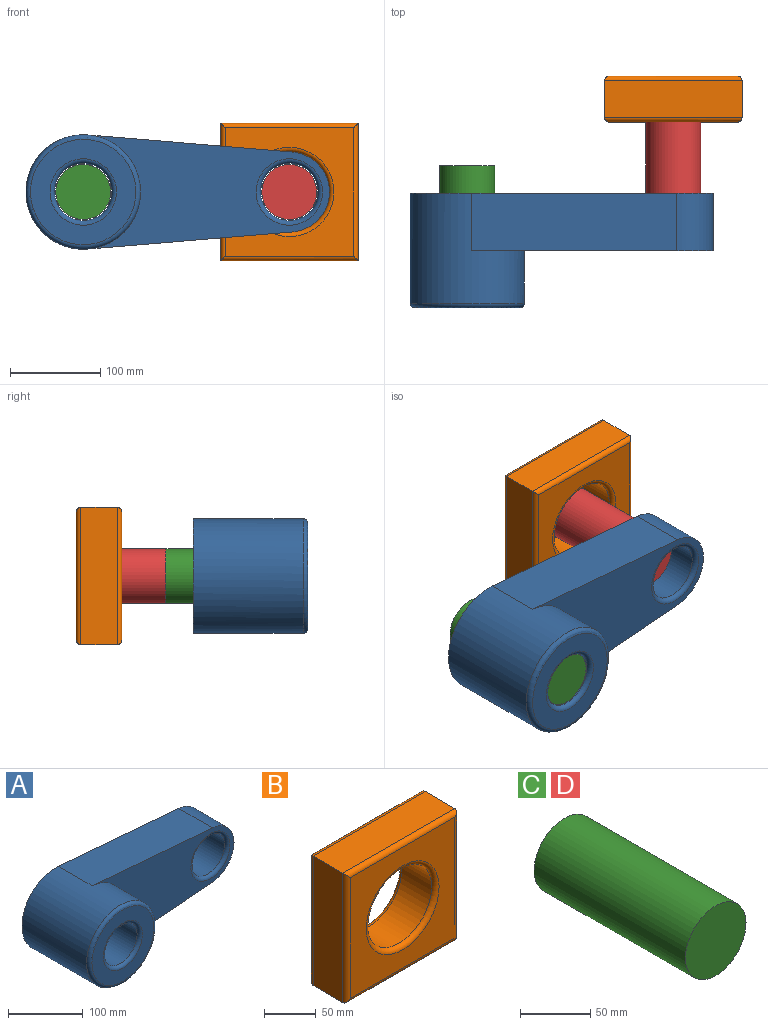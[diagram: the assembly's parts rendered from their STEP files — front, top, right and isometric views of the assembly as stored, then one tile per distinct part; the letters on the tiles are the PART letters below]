
ASSEMBLY  parts=4 mates=4
PART A: 12 faces, bbox 341.8x127x137.5 mm
  f0: plane 267.76x126.56mm, normal (0,-1,0), area 17271.4mm2, adj f1,f2,f3,f4,f11
  f1: cylinder r=63.5mm len=127mm, axis (0,1,0), area 36649.1mm2, adj f0,f2,f4,f7,f10
  f2: plane 227.01x63.5mm, normal (0.08,0,-1), area 14465.6mm2, adj f0,f1,f3,f7
  f3: cylinder r=44.45mm len=88.59mm, axis (0,1,0), area 8396.4mm2, adj f0,f2,f4,f7
  f4: plane 227.01x63.5mm, normal (0.08,0,1), area 14465.6mm2, adj f0,f1,f3,f7
  f5: cylinder r=31.75mm len=121.92mm, axis (0,1,0), area 24322mm2, adj f7,f9
  f6: cylinder r=31.75mm len=63.5mm, axis (0,1,0), area 11654.3mm2, adj f7,f11
  f7: plane 336.55x127mm, normal (0,1,0), area 27866.7mm2, adj f1,f2,f3,f4,f5,f6
  f8: plane 116.84x116.84mm, normal (0,-1,0), area 6460.5mm2, adj f9,f10
  f9: torus R=36.83mm, axis (0,-1,0), area 1684.4mm2, adj f5,f8
  f10: torus R=58.42mm, axis (0,-1,0), area 3091.2mm2, adj f1,f8
  f11: torus R=36.83mm, axis (0,-1,0), area 1684.4mm2, adj f0,f6
PART B: 17 faces, bbox 152.4x50.8x152.4 mm
  f0: plane 152.4x40.64mm, normal (0,0,1), area 6193.5mm2, adj f1,f3,f8,f13
  f1: plane 152.4x40.64mm, normal (-1,0,0), area 6193.5mm2, adj f0,f2,f9,f14
  f2: plane 152.4x40.64mm, normal (0,0,-1), area 6193.5mm2, adj f1,f3,f11,f16
  f3: plane 152.4x40.64mm, normal (1,0,0), area 6193.5mm2, adj f0,f2,f10,f15
  f4: plane 142.24x142.24mm, normal (0,-1,0), area 12525.2mm2, adj f7,f8,f9,f10,f11
  f5: plane 142.24x142.24mm, normal (0,1,0), area 12525.2mm2, adj f12,f13,f14,f15,f16
  f6: cylinder r=44.45mm len=88.9mm, axis (0,-1,0), area 11350.2mm2, adj f7,f12
  f7: torus R=49.53mm, axis (0,-1,0), area 2321.2mm2, adj f4,f6
  f8: cylinder r=5.08mm len=152.4mm, axis (1,0,0), area 1186.6mm2, adj f0,f4,f9,f10
  f9: cylinder r=5.08mm len=152.4mm, axis (0,0,1), area 1186.6mm2, adj f1,f4,f8,f11
  f10: cylinder r=5.08mm len=152.4mm, axis (0,0,-1), area 1186.6mm2, adj f3,f4,f8,f11
  f11: cylinder r=5.08mm len=152.4mm, axis (-1,0,0), area 1186.6mm2, adj f2,f4,f9,f10
  f12: torus R=49.53mm, axis (0,-1,0), area 2321.2mm2, adj f5,f6
  f13: cylinder r=5.08mm len=152.4mm, axis (-1,0,0), area 1186.6mm2, adj f0,f5,f14,f15
  f14: cylinder r=5.08mm len=152.4mm, axis (0,0,-1), area 1186.6mm2, adj f1,f5,f13,f16
  f15: cylinder r=5.08mm len=152.4mm, axis (0,0,1), area 1186.6mm2, adj f3,f5,f13,f16
  f16: cylinder r=5.08mm len=152.4mm, axis (1,0,0), area 1186.6mm2, adj f2,f5,f14,f15
PART C: 3 faces, bbox 61x152.4x61 mm
  f0: plane 60.96x60.96mm, normal (0,-1,0), area 2918.6mm2, adj f1
  f1: cylinder r=30.48mm len=152.4mm, axis (0,1,0), area 29186.4mm2, adj f0,f2
  f2: plane 60.96x60.96mm, normal (0,1,0), area 2918.6mm2, adj f1
PART D: same geometry as C
PLACE A t=(245.23,190.13,56)mm
PLACE B t=(473.83,320.09,56)mm
PLACE C t=(245.23,169.81,56)mm
PLACE D t=(473.83,264.21,56)mm
MATE planar C.f1 <-> A.f5  axis (0,-1,0) through (245.23,68.21,56)mm
MATE revolute D.f1 <-> B.f6  axis (0,1,0) through (473.83,315.01,56)mm
MATE cylindrical C.f1 <-> A.f5  axis (0,-1,0) through (245.23,68.21,56)mm
MATE cylindrical A.f6 <-> D.f1  axis (0,1,0) through (473.83,131.71,56)mm
